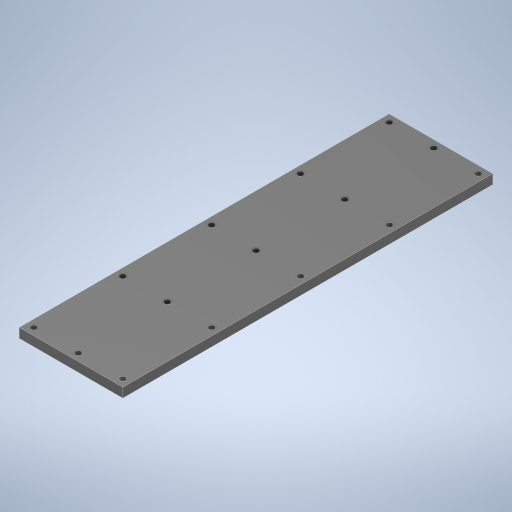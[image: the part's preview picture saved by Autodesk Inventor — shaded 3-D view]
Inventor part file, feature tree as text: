
AUTODESK INVENTOR PART (.ipt)
format: ipt  version: 2023 (Build 270158000, 158)  size: 253,440 bytes
history: native  units: in
note: dims shown in document units (in); Inventor stores cm internally (conversion verified against a paired STEP export)
features: sketch x2, extrude x1, hole x1
ambient origin geometry x8: Origin, YZ Plane, XZ Plane, XY Plane, X Axis, Y Axis, Z Axis, Center Point
bodies: Solid1 (feature_tree)
feature tree (4):
  extrude  "Extrusion1"  Depth=4.9213in
  hole  "Hole1"  [1 undecoded]
  sketch  "Sketch1"  dims[d0=1.378in d1=4.9213in]
  sketch  "Sketch2"  dims[d2=0.125in d3=0.0in d4=0.0984in d5=0.0984in d6=0.0984in d7=1.9685in d9=1.1811in d10=0.3937in d12=0.3937in d14=0.081in d15=0.146in d16=0.146in d17=0.25in d18=0.5635in d19=0.315in d20=0.8108in]
note: 1 required parameter value undecoded (feature->parameter linkage not recoverable at this tier; creation-order binding heuristic only, values carry confidence <= 0.55)
